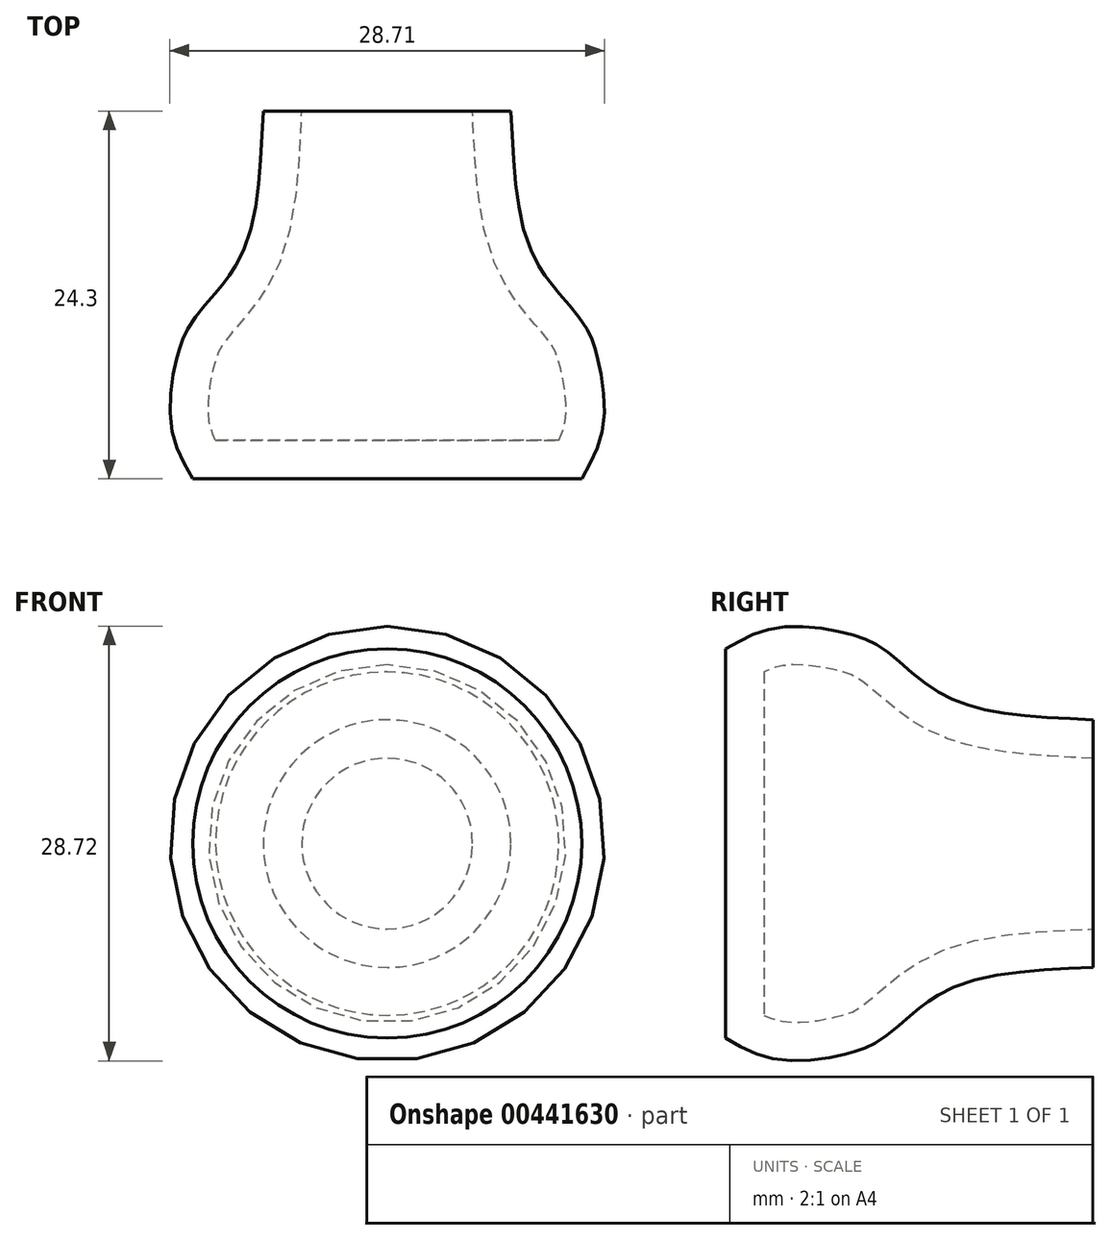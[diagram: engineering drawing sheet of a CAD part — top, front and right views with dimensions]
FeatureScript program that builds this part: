
annotation { "Feature Type Name" : "Feature", "Feature Type Description" : "" }
export const myFeature = defineFeature(function(context is Context, id is Id, definition is map)
    precondition{}
    {
        {
            var Q0;
            Q0=qCreatedBy(makeId("Top.planeOp"),FACE);
            var sketch = newSketch(context, id + "F0", { "sketchPlane" : qUnion([Q0])});
            skLineSegment(sketch, "E0", {"start": v(0, -18.39) * mm, "end": v(0, -19.04) * mm});
            skFitSpline(sketch, "E1", {"points": [v(0, 9.21) * mm, v(44.17, 9.67) * mm, v(53.35, 4.62) * mm, v(59.77, -3.18) * mm, v(60.23, -13.5) * mm, v(-6.77, -18.1) * mm], "startDerivative": vector(193.96, 14.31) * mm, "endDerivative": vector(-271.56, 11.98) * mm});
            skFitSpline(sketch, "E2", {"points": [v(-2.87, -14.2) * mm, v(3.79, -25.43) * mm], "startDerivative": vector(6.65, -11.24) * mm, "endDerivative": vector(6.65, -11.24) * mm});
            skPoint(sketch, "E3.orphan", {"position": v(0, 41.33) * mm});
            skLineSegment(sketch, "E4", {"start": v(-40.9, 54.02) * mm, "end": v(-40.9, 28.91) * mm});
            skLineSegment(sketch, "E5", {"start": v(-40.9, 54.02) * mm, "end": v(-32.7, 54.02) * mm});
            skFitSpline(sketch, "E6", {"points": [v(-32.7, 54.02) * mm, v(-32.05, 46.9) * mm, v(-30.42, 43.1) * mm, v(-28.03, 40.14) * mm, v(-27.02, 37.8) * mm, v(-26.6, 33.23) * mm, v(-28.03, 29.72) * mm], "startDerivative": vector(1.6, -35.5) * mm, "endDerivative": vector(-11.7, -20.55) * mm});
            skLineSegment(sketch, "E7", {"start": v(-28.03, 29.72) * mm, "end": v(-40.9, 29.72) * mm});
            skLineSegment(sketch, "E8", {"start": v(-40.9, 54.02) * mm, "end": v(-40.9, 60.14) * mm});
            skLineSegment(sketch, "E9", {"start": v(-40.9, 60.14) * mm, "end": v(-40.9, 19.9) * mm});
            skSolve(sketch);
        }
        {
            var Q0;
            {var subQ0=sQuery(id+"F0.wireOp",EDGE,"E5");Q0=makeQuery(id+"F0.imprint","IMPRINT",FACE,{"disambiguationData":[TD([[makeQuery(id+"F0.imprint","IMPRINT",EDGE,{"derivedFrom":subQ0}),-1.0]])]});}
            var Q1;
            Q1=sQuery(id+"F0.wireOp",EDGE,"E9");
            revolve(context, id + "F1", {"entities" : qUnion([Q0]), "axis" : qUnion([Q1]), "revolveType" : RevolveType.FULL});
        }
        {
            var Q0;
            Q0=makeQuery(id+"F1.opRevolve","SWEPT_FACE",FACE,{"disambiguationData":[OSD([sQuery(id+"F0.wireOp",EDGE,"E5")])]});
            shell(context, id + "F2", {"entities" : qUnion([Q0]), "thickness" : 2.54 * mm});
        }
    });
